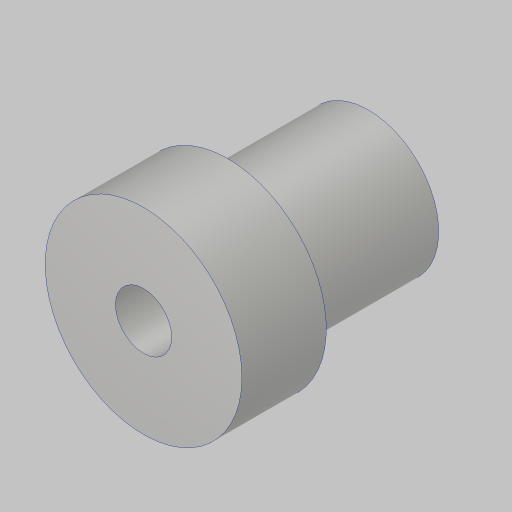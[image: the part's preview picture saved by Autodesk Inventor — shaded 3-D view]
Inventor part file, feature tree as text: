
AUTODESK INVENTOR PART (.ipt)
format: ipt  version: 2023.5 (Build 275446000, 446)  size: 119,808 bytes
history: native  units: in
note: dims shown in document units (in); Inventor stores cm internally (conversion verified against a paired STEP export)
features: sketch x3, extrude x2, hole x1, projected_geometry x1
ambient origin geometry x8: Origin, YZ Plane, XZ Plane, XY Plane, X Axis, Y Axis, Z Axis, Center Point
bodies: Solid1 (feature_tree)
feature tree (7):
  extrude  "Extrusion1"  Depth=1.0in TaperAngle=0.0deg
  extrude  "Extrusion3"  Depth=0.625in TaperAngle=0.0deg
  hole  "Hole2"  [1 undecoded]
  sketch  "Sketch1"  dims[d0=0.875in d1=1.0in d2=0.0in]
  sketch  "Sketch3"  dims[d6=0.625in d7=0.625in d8=0.0in]
  projected_geometry  "Projected Loop2"
  sketch  "Sketch5"  dims[d17=0.25in d18=0.75in d19=0.279in d20=0.25in d21=0.5635in d22=1.0in d23=0.8108in]
note: 1 required parameter value undecoded (feature->parameter linkage not recoverable at this tier; creation-order binding heuristic only, values carry confidence <= 0.55)
